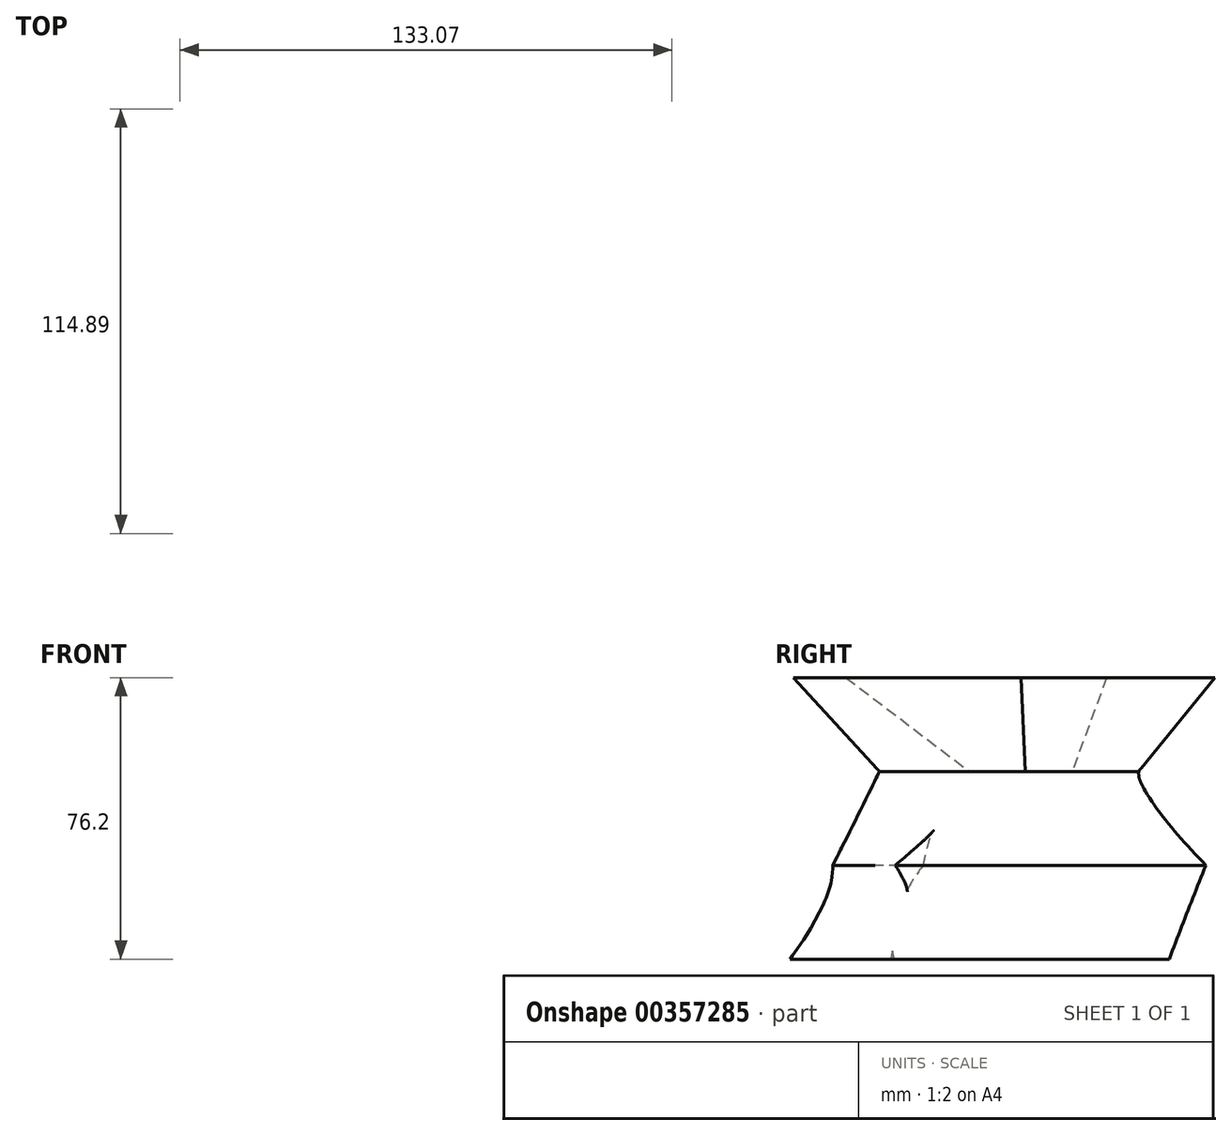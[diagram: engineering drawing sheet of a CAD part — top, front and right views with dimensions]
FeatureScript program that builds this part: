
annotation { "Feature Type Name" : "Feature", "Feature Type Description" : "" }
export const myFeature = defineFeature(function(context is Context, id is Id, definition is map)
    precondition{}
    {
        {
            var Q0;
            Q0=qCreatedBy(makeId("Top.planeOp"),FACE);
            var sketch = newSketch(context, id + "F0", { "sketchPlane" : qUnion([Q0])});
            skFitSpline(sketch, "E0", {"points": [v(-32.65, 34.54) * mm, v(-22.15, -16.47) * mm, v(-46.93, -28.42) * mm, v(20.99, -35.41) * mm, v(17.78, -55.23) * mm, v(46.05, -30.17) * mm, v(29.44, 20.55) * mm, v(51.88, 27.54) * mm, v(12.82, 44.74) * mm, v(-32.65, 34.54) * mm]});
            skSolve(sketch);
        }
        {
            var Q0;
            Q0=qCreatedBy(makeId("Top.planeOp"),FACE);
            cPlane(context, id + "F1", {"entities" : qUnion([Q0]), "cplaneType" : CPlaneType.OFFSET, "offset" : 25.4 * mm, "width" : 152.4 * mm, "height" : 152.4 * mm});
        }
        {
            var Q0;
            Q0=qCreatedBy(id+"F1.planeOp",FACE);
            var sketch = newSketch(context, id + "F2", { "sketchPlane" : qUnion([Q0])});
            skFitSpline(sketch, "E1", {"points": [v(-30.98, 47.64) * mm, v(-15.62, 23.82) * mm, v(-37.86, 7.67) * mm, v(-8.47, -23.04) * mm, v(-33.36, -37.6) * mm, v(10.06, -43.69) * mm, v(15.09, -36.8) * mm, v(25.15, -19.86) * mm, v(48.18, -27) * mm, v(47.91, 9.79) * mm, v(27.8, 26.2) * mm, v(30.44, 50.29) * mm, v(-30.98, 47.64) * mm]});
            skSolve(sketch);
        }
        {
            var Q0;
            Q0=makeQuery(id+"F2.imprint","IMPRINT",FACE,{"disambiguationData":[TD([[makeQuery(id+"F2.imprint","IMPRINT",EDGE,{"derivedFrom":sQuery(id+"F2.wireOp",EDGE,"E1")}),1.0]])]});
            var Q1;
            Q1=makeQuery(id+"F0.imprint","IMPRINT",FACE,{"disambiguationData":[TD([[makeQuery(id+"F0.imprint","IMPRINT",EDGE,{"derivedFrom":sQuery(id+"F0.wireOp",EDGE,"E0")}),1.0]])]});
            loft(context, id + "F3", {"sheetProfilesArray" : [{ "sheetProfileEntities" : qUnion([Q0]) }, { "sheetProfileEntities" : qUnion([Q1]) }]});
        }
        {
            var Q0;
            Q0=qCreatedBy(id+"F1.planeOp",FACE);
            cPlane(context, id + "F4", {"entities" : qUnion([Q0]), "cplaneType" : CPlaneType.OFFSET, "offset" : 25.4 * mm, "width" : 152.4 * mm, "height" : 152.4 * mm});
        }
        {
            var Q0;
            Q0=qCreatedBy(id+"F4.planeOp",FACE);
            var sketch = newSketch(context, id + "F5", { "sketchPlane" : qUnion([Q0])});
            skFitSpline(sketch, "E2", {"points": [v(72.08, 31.37) * mm, v(-52.43, 30.93) * mm, v(-56.7, 25.3) * mm, v(-55.58, 19.91) * mm, v(-52.88, 14.97) * mm, v(-60.3, 7.1) * mm, v(-46.81, -7.06) * mm, v(-57.15, -19.42) * mm, v(60.62, -25.04) * mm, v(56.35, 3.73) * mm, v(72.08, 31.37) * mm]});
            skSolve(sketch);
        }
        {
            var Q1;
            Q1=makeQuery(id+"F5.imprint","IMPRINT",FACE,{"disambiguationData":[TD([[makeQuery(id+"F5.imprint","IMPRINT",EDGE,{"derivedFrom":sQuery(id+"F5.wireOp",EDGE,"E2")}),1.0]])]});
            var Q2;
            Q2=makeQuery(id+"F3.opLoft","CAP_FACE",FACE,{"disambiguationData":[OSD([makeQuery(id+"F2.imprint","IMPRINT",FACE,{"disambiguationData":[TD([[makeQuery(id+"F2.imprint","IMPRINT",EDGE,{"derivedFrom":sQuery(id+"F2.wireOp",EDGE,"E1")}),1.0]])]})])],"isStart":true});
            loft(context, id + "F6", {"operationType" : NewBodyOperationType.ADD, "sheetProfilesArray" : [{ "sheetProfileEntities" : qUnion([Q1]) }, { "sheetProfileEntities" : qUnion([Q2]) }]});
        }
        {
            var Q0;
            Q0=qCreatedBy(id+"F4.planeOp",FACE);
            cPlane(context, id + "F7", {"entities" : qUnion([Q0]), "cplaneType" : CPlaneType.OFFSET, "offset" : 25.4 * mm, "width" : 152.4 * mm, "height" : 152.4 * mm});
        }
        {
            var Q0;
            Q0=qCreatedBy(id+"F7.planeOp",FACE);
            var sketch = newSketch(context, id + "F8", { "sketchPlane" : qUnion([Q0])});
            skCircle(sketch, "E3.cCircle", {"center": v(0, 0) * mm, "radius": 48.8 * mm, "construction": true});
            skLineSegment(sketch, "E3.0", {"start": v(59.95, 6.68) * mm, "end": v(24.88, -54.96) * mm});
            skLineSegment(sketch, "E3.1", {"start": v(24.88, -54.96) * mm, "end": v(-44.58, -40.64) * mm});
            skLineSegment(sketch, "E3.2", {"start": v(-44.58, -40.64) * mm, "end": v(-52.43, 29.84) * mm});
            skLineSegment(sketch, "E3.3", {"start": v(-52.43, 29.84) * mm, "end": v(12.18, 59.08) * mm});
            skLineSegment(sketch, "E3.4", {"start": v(12.18, 59.08) * mm, "end": v(59.95, 6.68) * mm});
            skPoint(sketch, "E3.0.midPoint", {"position": v(42.41, -24.14) * mm});
            skSolve(sketch);
        }
        {
            var Q1;
            Q1=makeQuery(id+"F8.imprint","IMPRINT",FACE,{"disambiguationData":[TD([[makeQuery(id+"F8.imprint","IMPRINT",EDGE,{"derivedFrom":sQuery(id+"F8.wireOp",EDGE,"E3.0")}),-1.0]])]});
            var Q2;
            Q2=makeQuery(id+"F6.opLoft","CAP_FACE",FACE,{"disambiguationData":[OSD([makeQuery(id+"F5.imprint","IMPRINT",FACE,{"disambiguationData":[TD([[makeQuery(id+"F5.imprint","IMPRINT",EDGE,{"derivedFrom":sQuery(id+"F5.wireOp",EDGE,"E2")}),1.0]])]})])],"isStart":true});
            loft(context, id + "F9", {"operationType" : NewBodyOperationType.ADD, "sheetProfilesArray" : [{ "sheetProfileEntities" : qUnion([Q1]) }, { "sheetProfileEntities" : qUnion([Q2]) }]});
        }
    });
